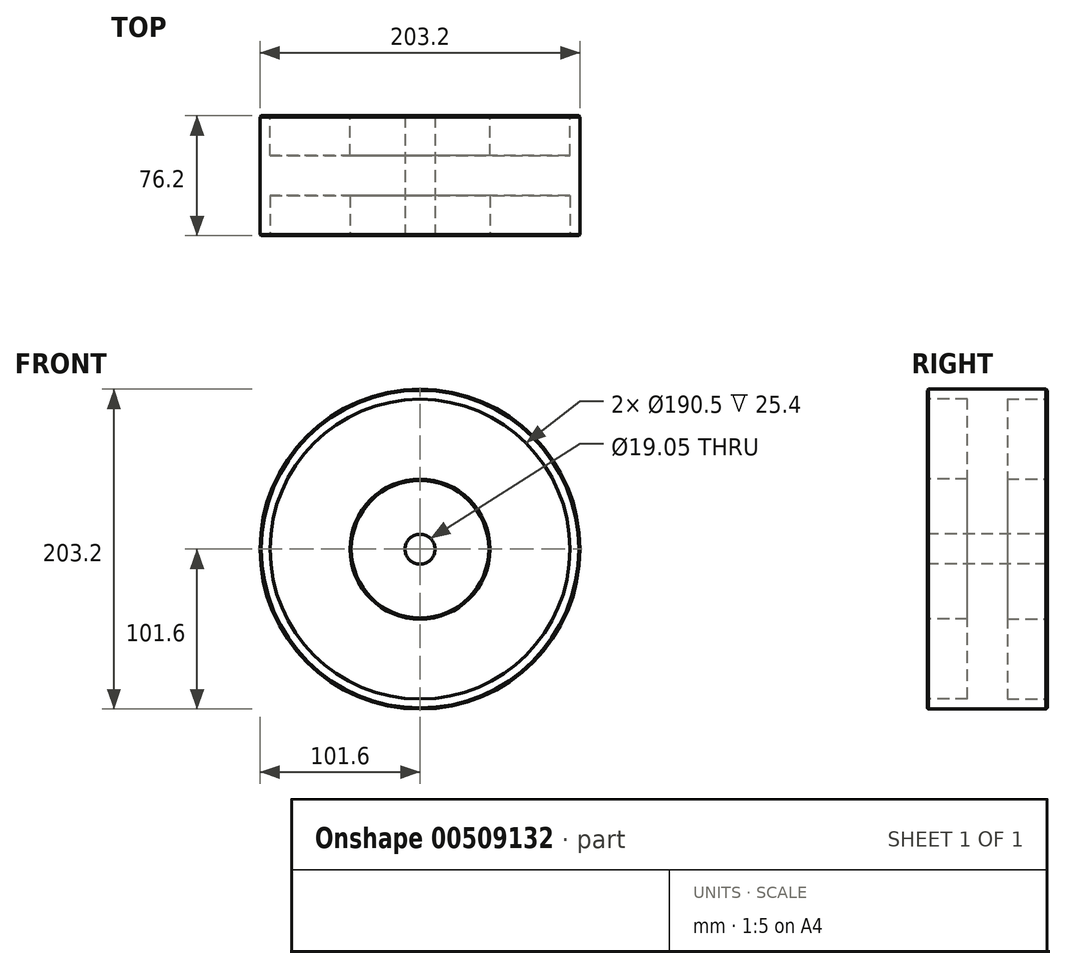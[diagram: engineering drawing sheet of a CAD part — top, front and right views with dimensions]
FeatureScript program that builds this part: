
annotation { "Feature Type Name" : "Feature", "Feature Type Description" : "" }
export const myFeature = defineFeature(function(context is Context, id is Id, definition is map)
    precondition{}
    {
        {
            var Q0;
            Q0=qCreatedBy(makeId("Front.planeOp"),FACE);
            var sketch = newSketch(context, id + "F0", { "sketchPlane" : qUnion([Q0])});
            skCircle(sketch, "E0", {"center": v(0, 0) * mm, "radius": 101.6 * mm});
            skSolve(sketch);
        }
        {
            var Q0;
            Q0=makeQuery(id+"F0.imprint","IMPRINT",FACE,{"disambiguationData":[TD([[makeQuery(id+"F0.imprint","IMPRINT",EDGE,{"derivedFrom":sQuery(id+"F0.wireOp",EDGE,"E0")}),1.0]])]});
            extrude(context, id + "F1", {"entities" : qUnion([Q0]), "endBound" : BoundingType.SYMMETRIC, "depth" : 76.2 * mm});
        }
        {
            var Q0;
            Q0=makeQuery(id+"F1.opExtrude","CAP_FACE",FACE,{"disambiguationData":[OSD([sQuery(id+"F0.wireOp",EDGE,"E0")])],"isStart":false});
            var sketch = newSketch(context, id + "F2", { "sketchPlane" : qUnion([Q0])});
            skCircle(sketch, "E1", {"center": v(0, 0) * mm, "radius": 44.45 * mm});
            skCircle(sketch, "E2", {"center": v(0, 0) * mm, "radius": 95.25 * mm});
            skSolve(sketch);
        }
        {
            var Q0;
            Q0=makeQuery(id+"F2.imprint","IMPRINT",FACE,{"disambiguationData":[TD([[makeQuery(id+"F2.imprint","IMPRINT",EDGE,{"derivedFrom":sQuery(id+"F2.wireOp",EDGE,"E1")}),-1.0]])]});
            extrude(context, id + "F3", {"entities" : qUnion([Q0]), "operationType" : NewBodyOperationType.REMOVE, "oppositeDirection" : true, "depth" : 25.4 * mm});
        }
        {
            var Q0;
            Q0=makeQuery(id+"F1.opExtrude","CAP_FACE",FACE,{"disambiguationData":[OSD([sQuery(id+"F0.wireOp",EDGE,"E0")])],"isStart":true});
            var sketch = newSketch(context, id + "F4", { "sketchPlane" : qUnion([Q0])});
            skCircle(sketch, "E3", {"center": v(0, 0) * mm, "radius": 44.45 * mm});
            skCircle(sketch, "E4", {"center": v(0, 0) * mm, "radius": 95.25 * mm});
            skSolve(sketch);
        }
        {
            var Q0;
            Q0=makeQuery(id+"F4.imprint","IMPRINT",FACE,{"disambiguationData":[TD([[makeQuery(id+"F4.imprint","IMPRINT",EDGE,{"derivedFrom":sQuery(id+"F4.wireOp",EDGE,"E3")}),-1.0]])]});
            extrude(context, id + "F5", {"entities" : qUnion([Q0]), "operationType" : NewBodyOperationType.REMOVE, "oppositeDirection" : true, "depth" : 25.4 * mm});
        }
        {
            var Q0;
            Q0=makeQuery(id+"F3.boolean.opBoolean","SPLIT",FACE,{"disambiguationData":[TD([makeQuery(id+"F3.opExtrude","SWEPT_FACE",FACE,{"disambiguationData":[OSD([sQuery(id+"F2.wireOp",EDGE,"E1")])]})])],"derivedFrom":makeQuery(id+"F1.opExtrude","CAP_FACE",FACE,{"disambiguationData":[OSD([sQuery(id+"F0.wireOp",EDGE,"E0")])],"isStart":false})});
            var sketch = newSketch(context, id + "F6", { "sketchPlane" : qUnion([Q0])});
            skCircle(sketch, "E5", {"center": v(0, 0) * mm, "radius": 9.53 * mm});
            skSolve(sketch);
        }
        {
            var Q0;
            Q0=sQuery(id+"F6.wireOp",VERTEX,"E5.center");
            var Q1;
            Q1=makeQuery(id+"F1.opExtrude","SWEPT_BODY",BODY,{"disambiguationData":[OSD([sQuery(id+"F0.wireOp",EDGE,"E0")])]});
            hole(context, id + "F7", {"style" : HoleStyle.SIMPLE, "endStyle" : HoleEndStyle.THROUGH, "holeDiameter" : 19.05 * mm, "isTappedThrough" : true, "tappedDepth" : 12.7 * mm, "tapClearance" : 3, "locations" : qUnion([Q0]), "scope" : qUnion([Q1])});
        }
        {
            var Q0;
            Q0=makeQuery(id+"F7.hole-0.boolean.opBoolean","COPY",EDGE,{"derivedFrom":makeQuery(id+"F7.hole-0.opRevolve","SWEPT_EDGE",EDGE,{"disambiguationData":[OSD([sQuery(id+"F7.hole-0.sketch.wireOp",EDGE,"core_line_2"),sQuery(id+"F7.hole-0.sketch.wireOp",EDGE,"core_line_3")])]})});
            var Q1;
            Q1=makeQuery(id+"F3.boolean.opBoolean","COPY",EDGE,{"derivedFrom":makeQuery(id+"F3.opExtrude","CAP_EDGE",EDGE,{"disambiguationData":[OSD([sQuery(id+"F2.wireOp",EDGE,"E1")])],"isStart":true})});
            var Q2;
            Q2=makeQuery(id+"F3.boolean.opBoolean","COPY",EDGE,{"derivedFrom":makeQuery(id+"F3.opExtrude","CAP_EDGE",EDGE,{"disambiguationData":[OSD([sQuery(id+"F2.wireOp",EDGE,"E2")])],"isStart":true})});
            var Q3;
            Q3=makeQuery(id+"F1.opExtrude","CAP_EDGE",EDGE,{"disambiguationData":[OSD([sQuery(id+"F0.wireOp",EDGE,"E0")])],"isStart":false});
            var Q4;
            Q4=makeQuery(id+"F7.hole-0.boolean.opBoolean","INTERSECT",EDGE,{"derivedFrom":[makeQuery(id+"F5.boolean.opBoolean","SPLIT",FACE,{"disambiguationData":[TD([makeQuery(id+"F5.opExtrude","SWEPT_FACE",FACE,{"disambiguationData":[OSD([sQuery(id+"F4.wireOp",EDGE,"E3")])]})])],"derivedFrom":makeQuery(id+"F1.opExtrude","CAP_FACE",FACE,{"disambiguationData":[OSD([sQuery(id+"F0.wireOp",EDGE,"E0")])],"isStart":true})}),makeQuery(id+"F7.hole-0.opRevolve","SWEPT_FACE",FACE,{"disambiguationData":[OSD([sQuery(id+"F7.hole-0.sketch.wireOp",EDGE,"core_line_2")])]})]});
            var Q5;
            Q5=makeQuery(id+"F5.boolean.opBoolean","COPY",EDGE,{"derivedFrom":makeQuery(id+"F5.opExtrude","CAP_EDGE",EDGE,{"disambiguationData":[OSD([sQuery(id+"F4.wireOp",EDGE,"E3")])],"isStart":true})});
            var Q6;
            Q6=makeQuery(id+"F5.boolean.opBoolean","COPY",EDGE,{"derivedFrom":makeQuery(id+"F5.opExtrude","CAP_EDGE",EDGE,{"disambiguationData":[OSD([sQuery(id+"F4.wireOp",EDGE,"E4")])],"isStart":true})});
            var Q7;
            Q7=makeQuery(id+"F1.opExtrude","CAP_EDGE",EDGE,{"disambiguationData":[OSD([sQuery(id+"F0.wireOp",EDGE,"E0")])],"isStart":true});
            chamfer(context, id + "F8", {"entities" : qUnion([Q0, Q1, Q2, Q3, Q4, Q5, Q6, Q7]), "width" : 0.76 * mm, "tangentPropagation" : true});
        }
    });
